# Revit family: 9.Пластинчатый шумоглушитель для прямоугольных каналов SG
name_source: partatom
category: Оборудование
revit_build: Autodesk Revit 2016 (Build: 20151209_0715(x64)
units: mm (PartAtom-declared; Revit-internal decimal feet)

## family parameters
Всегда вертикально = Да
На основе рабочей плоскости = Нет
Общий = Нет
При загрузке вырезать с полостями = Нет
Размер круглого соединителя = Использовать диаметр
Тип детали = Нормальный
Точка расчета площади = Нет

## types (20) — shared parameters
Глубина среза = 15 мм
Единица измерения = шт.
Завод изготовитель = KORF
Ключевая пометка = Вентиляция
Материал = Сталь серая
Наименование и тех.хар-ка = Пластинчатый шумоглушитель для прямоугольных каналов
Отступ = 20 мм
Раздел = ОВ

## per-type parameters (varying)
| type | А | Б | Высота | Г | Д | Е | Ж | И | Масса единицы | Размер В | Тип, марка, обозначение | Ширина |
| 30-15/6 | 300 мм | 150 мм | 150 мм | 170 мм | 340 мм | 190 мм | 9 мм | 614 мм | 8.5 кг | 320 мм | SG 30-15/6 | 300 мм |
| 40-20/6 | 400 мм | 200 мм | 200 мм | 220 мм | 440 мм | 240 мм | 9 мм | 614 мм | 10.7 кг | 420 мм | SG 40-20/6 | 400 мм |
| 50-25/6 | 500 мм | 250 мм | 250 мм | 270 мм | 540 мм | 290 мм | 9 мм | 614 мм | 15 кг | 520 мм | SG 50-25/6 | 500 мм |
| 50-30/6 | 500 мм | 300 мм | 300 мм | 320 мм | 540 мм | 340 мм | 9 мм | 614 мм | 15.8 кг | 520 мм | SG 50-30/6 | 500 мм |
| 60-30/6 | 600 мм | 300 мм | 300 мм | 320 мм | 640 мм | 340 мм | 9 мм | 614 мм | 17.4 кг | 620 мм | SG 60-30/6 | 600 мм |
| 60-35/6 | 600 мм | 350 мм | 350 мм | 370 мм | 640 мм | 390 мм | 9 мм | 614 мм | 19.2 кг | 620 мм | SG 60-35/6 | 600 мм |
| 70-40/6 | 700 мм | 400 мм | 400 мм | 420 мм | 740 мм | 440 мм | 9 мм | 614 мм | 23.5 кг | 720 мм | SG 70-40/6 | 700 мм |
| 80-50/6 | 800 мм | 500 мм | 500 мм | 520 мм | 870 мм | 540 мм | 9 мм | 614 мм | 27.5 кг | 820 мм | SG 80-50/6 | 800 мм |
| 90-50/6 | 900 мм | 500 мм | 500 мм | 530 мм | 960 мм | 560 мм | 11 мм | 616 мм | 33 кг | 930 мм | SG 90-50/6 | 900 мм |
| 100-50/6 | 1000 мм | 500 мм | 500 мм | 530 мм | 1060 мм | 560 мм | 11 мм | 616 мм | 34.4 кг | 1030 мм | SG 100-50/6 | 1000 мм |
| 30-15 | 300 мм | 150 мм | 150 мм | 170 мм | 340 мм | 190 мм | 9 мм | 1014 мм | 14.2 кг | 320 мм | SG 30-15 | 300 мм |
| 40-20 | 400 мм | 200 мм | 200 мм | 220 мм | 440 мм | 240 мм | 9 мм | 1014 мм | 17.8 кг | 420 мм | SG 40-20 | 400 мм |
| 50-25 | 500 мм | 250 мм | 250 мм | 270 мм | 540 мм | 290 мм | 9 мм | 1014 мм | 25 кг | 520 мм | SG 50-25 | 500 мм |
| 50-30 | 500 мм | 300 мм | 300 мм | 320 мм | 540 мм | 340 мм | 9 мм | 1014 мм | 26.4 кг | 520 мм | SG 50-30 | 500 мм |
| 60-30 | 600 мм | 300 мм | 300 мм | 320 мм | 640 мм | 340 мм | 9 мм | 1014 мм | 29 кг | 620 мм | SG 60-30 | 600 мм |
| 60-35 | 600 мм | 350 мм | 350 мм | 370 мм | 640 мм | 390 мм | 9 мм | 1014 мм | 32 кг | 620 мм | SG 60-35 | 600 мм |
| 70-40 | 700 мм | 400 мм | 400 мм | 420 мм | 740 мм | 440 мм | 9 мм | 1014 мм | 39.2 кг | 720 мм | SG 70-40 | 700 мм |
| 80-50 | 800 мм | 500 мм | 500 мм | 520 мм | 870 мм | 540 мм | 9 мм | 1014 мм | 45.8 кг | 820 мм | SG 80-50 | 800 мм |
| 90-50 | 900 мм | 500 мм | 500 мм | 530 мм | 960 мм | 560 мм | 11 мм | 1016 мм | 55 кг | 930 мм | SG 90-50 | 900 мм |
| 100-50 | 1000 мм | 500 мм | 500 мм | 530 мм | 1060 мм | 560 мм | 11 мм | 1016 мм | 57.4 кг | 1030 мм | SG 100-50 | 1000 мм |
